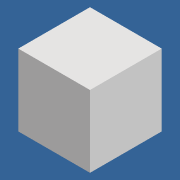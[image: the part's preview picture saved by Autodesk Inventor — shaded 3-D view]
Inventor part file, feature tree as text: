
AUTODESK INVENTOR PART (.ipt)
format: ipt  version: 2020 (Build 240168000, 168)  size: 74,752 bytes
history: native  units: mm
features: sketch x2, extrude x1
ambient origin geometry x8: Origin, YZ Plane, XZ Plane, XY Plane, X Axis, Y Axis, Z Axis, Center Point
bodies: Solid1 (feature_tree)
feature tree (3):
  extrude  "Extrusion1"  Depth=57.0mm
  sketch  "Sketch2"  dims[d2=57.0mm d3=0.0mm]
  sketch  "Sketch1"  dims[d0=57.0mm d1=57.0mm]
